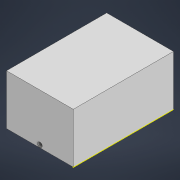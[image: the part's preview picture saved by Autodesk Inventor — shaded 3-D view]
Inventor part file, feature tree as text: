
AUTODESK INVENTOR PART (.ipt)
format: ipt  version: 2022 (Build 260153000, 153)  size: 106,496 bytes
history: native  units: mm
features: sketch x6, hole x3, extrude x1
ambient origin geometry x8: Origin, YZ Plane, XZ Plane, XY Plane, X Axis, Y Axis, Z Axis, Center Point
bodies: Solid1 (feature_tree)
feature tree (10):
  extrude  "Extrusion1"  Depth=150.0mm
  hole  "Hole1"  [1 undecoded]
  hole  "Hole2"  [1 undecoded]
  sketch  "Sketch4"  dims[d13=7.0mm d14=6.0mm d15=4.0mm d16=2.0mm d17=90.0deg d18=8.0mm d19=0.0mm d20=30.0mm]
  sketch  "Sketch5"  dims[d21=29.0mm d22=6.0mm d23=4.0mm d24=2.0mm d25=90.0deg d26=15.0mm d27=0.0mm]
  hole  "Hole3"  [1 undecoded]
  sketch  "Sketch1"  dims[d0=100.0mm d1=150.0mm]
  sketch  "Sketch2"  dims[d2=75.0mm d3=0.0mm]
  sketch  "Sketch3"  dims[d6=7.0mm d7=6.0mm d8=4.0mm d9=2.0mm d10=90.0deg d11=8.0mm d12=0.0mm]
  sketch  "Sketch6"
note: 3 required parameter values undecoded (feature->parameter linkage not recoverable at this tier; creation-order binding heuristic only, values carry confidence <= 0.55)
